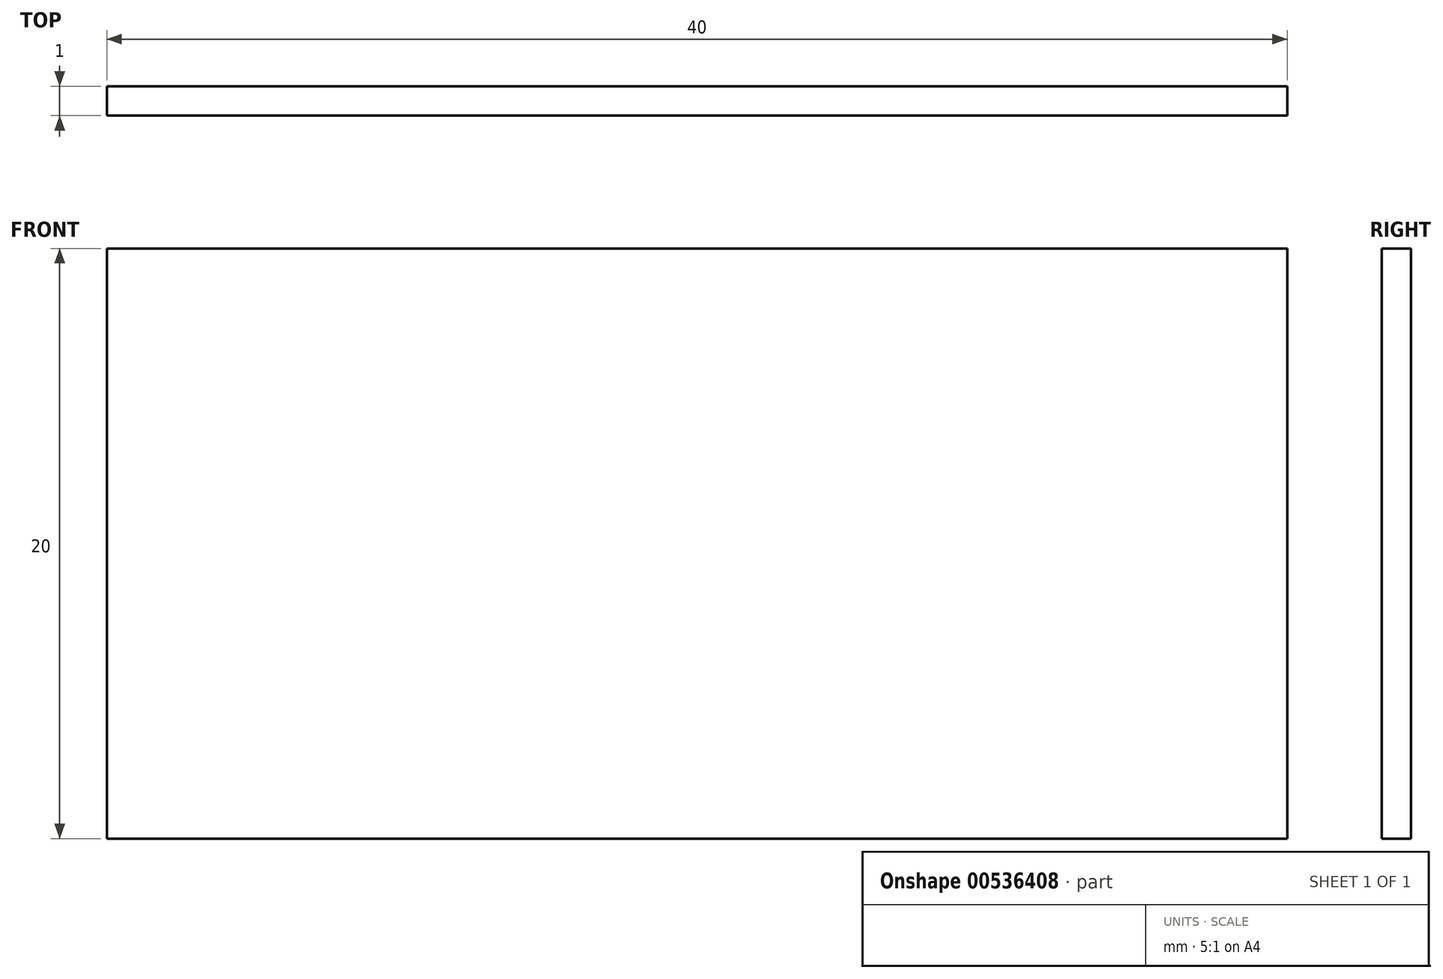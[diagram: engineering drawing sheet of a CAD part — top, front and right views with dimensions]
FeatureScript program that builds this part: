
annotation { "Feature Type Name" : "Feature", "Feature Type Description" : "" }
export const myFeature = defineFeature(function(context is Context, id is Id, definition is map)
    precondition{}
    {
        {
            var Q0;
            Q0=qCreatedBy(makeId("Front.planeOp"),FACE);
            var sketch = newSketch(context, id + "F0", { "sketchPlane" : qUnion([Q0])});
            skLineSegment(sketch, "E0.bottom", {"start": v(20, -10) * mm, "end": v(-20, -10) * mm});
            skLineSegment(sketch, "E0.top", {"start": v(20, 10) * mm, "end": v(-20, 10) * mm});
            skLineSegment(sketch, "E0.left", {"start": v(20, -10) * mm, "end": v(20, 10) * mm});
            skLineSegment(sketch, "E0.right", {"start": v(-20, -10) * mm, "end": v(-20, 10) * mm});
            skPoint(sketch, "E0.middle", {"position": v(0, 0) * mm});
            skSolve(sketch);
        }
        {
            var Q0;
            Q0=qSketchRegion(id+"F0",true);
            extrude(context, id + "F1", {"entities" : qUnion([Q0]), "depth" : 1 * mm});
        }
    });
